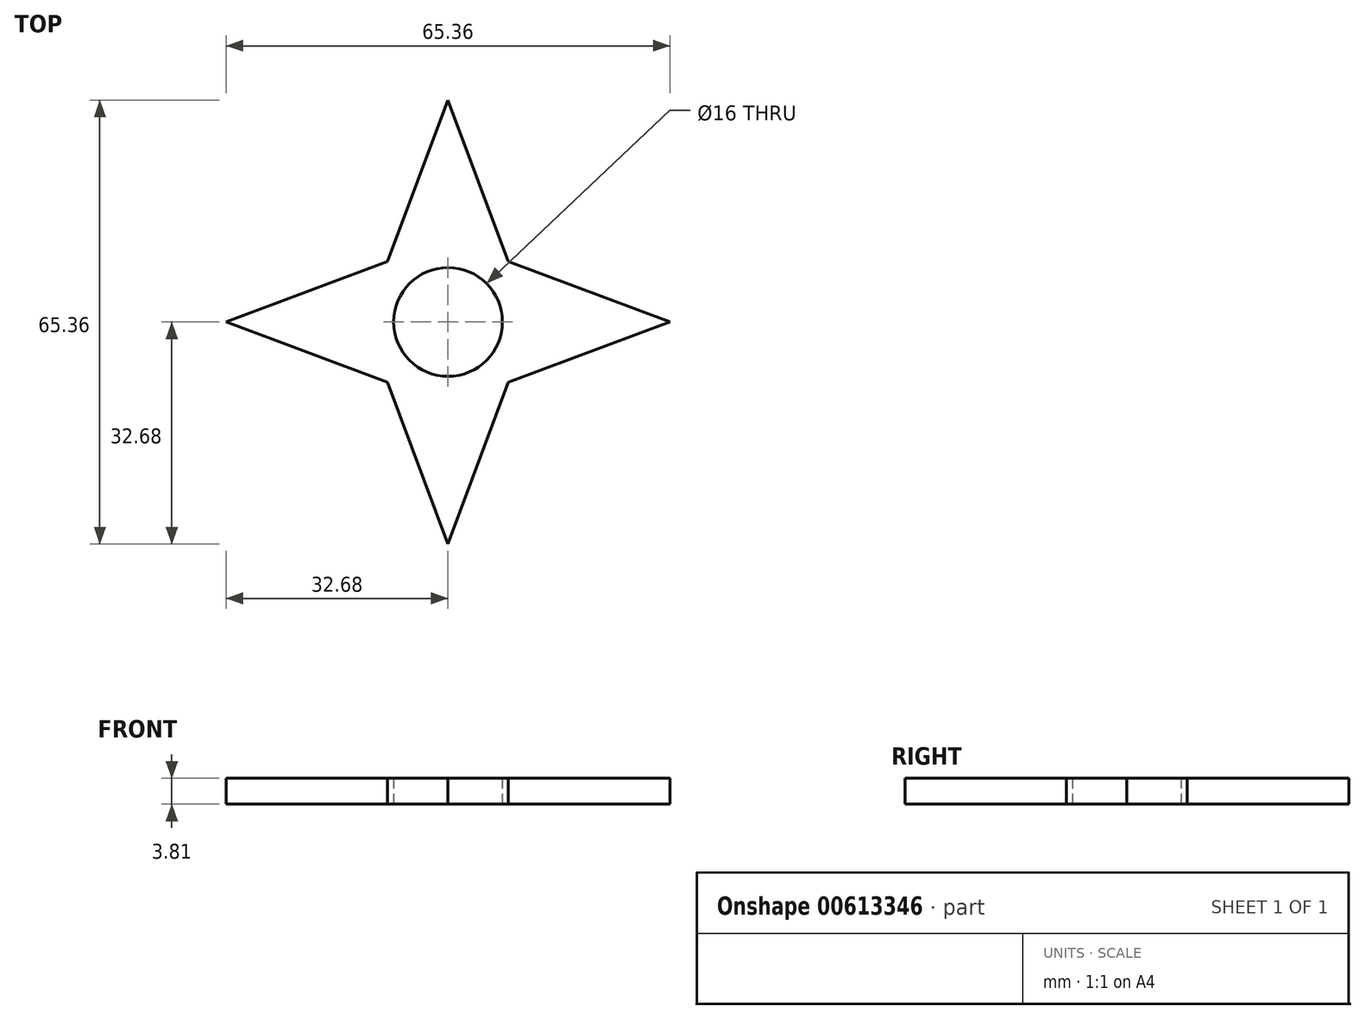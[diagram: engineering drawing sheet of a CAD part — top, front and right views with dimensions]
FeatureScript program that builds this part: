
annotation { "Feature Type Name" : "Feature", "Feature Type Description" : "" }
export const myFeature = defineFeature(function(context is Context, id is Id, definition is map)
    precondition{}
    {
        {
            var Q0;
            Q0=qCreatedBy(makeId("Top.planeOp"),FACE);
            var sketch = newSketch(context, id + "F0", { "sketchPlane" : qUnion([Q0])});
            skLineSegment(sketch, "E0.bottom", {"start": v(8.9, 8.9) * mm, "end": v(-8.9, 8.9) * mm});
            skLineSegment(sketch, "E0.top", {"start": v(8.9, -8.89) * mm, "end": v(-8.9, -8.89) * mm});
            skLineSegment(sketch, "E0.left", {"start": v(8.9, 8.9) * mm, "end": v(8.9, -8.89) * mm});
            skLineSegment(sketch, "E0.right", {"start": v(-8.9, 8.9) * mm, "end": v(-8.9, -8.89) * mm});
            skPoint(sketch, "E0.middle", {"position": v(0, 0) * mm});
            skLineSegment(sketch, "E1", {"start": v(-8.9, 8.9) * mm, "end": v(0, 32.68) * mm});
            skLineSegment(sketch, "E2", {"start": v(0, 32.68) * mm, "end": v(8.89, 8.9) * mm});
            skLineSegment(sketch, "E3", {"start": v(-8.89, 8.9) * mm, "end": v(-32.68, 0) * mm});
            skLineSegment(sketch, "E4", {"start": v(-32.68, 0) * mm, "end": v(-8.89, -8.9) * mm});
            skLineSegment(sketch, "E5", {"start": v(-8.9, -8.89) * mm, "end": v(0, -32.68) * mm});
            skLineSegment(sketch, "E6", {"start": v(0, -32.68) * mm, "end": v(8.89, -8.9) * mm});
            skLineSegment(sketch, "E7", {"start": v(8.9, -8.89) * mm, "end": v(32.68, 0) * mm});
            skLineSegment(sketch, "E8", {"start": v(32.68, 0) * mm, "end": v(8.9, 8.9) * mm});
            skCircle(sketch, "E9", {"center": v(0, 0) * mm, "radius": 8 * mm});
            skSolve(sketch);
        }
        {
            var Q0;
            Q0=makeQuery(id+"F0.imprint","IMPRINT",FACE,{"disambiguationData":[TD([[makeQuery(id+"F0.imprint","IMPRINT",EDGE,{"derivedFrom":sQuery(id+"F0.wireOp",EDGE,"E0.bottom")}),-1.0]])]});
            var Q1;
            Q1=makeQuery(id+"F0.imprint","IMPRINT",FACE,{"disambiguationData":[TD([[makeQuery(id+"F0.imprint","IMPRINT",EDGE,{"derivedFrom":sQuery(id+"F0.wireOp",EDGE,"E0.right")}),-1.0]])]});
            var Q2;
            Q2=makeQuery(id+"F0.imprint","IMPRINT",FACE,{"disambiguationData":[TD([[makeQuery(id+"F0.imprint","IMPRINT",EDGE,{"derivedFrom":sQuery(id+"F0.wireOp",EDGE,"E0.top")}),1.0]])]});
            var Q3;
            Q3=makeQuery(id+"F0.imprint","IMPRINT",FACE,{"disambiguationData":[TD([[makeQuery(id+"F0.imprint","IMPRINT",EDGE,{"derivedFrom":sQuery(id+"F0.wireOp",EDGE,"E0.left")}),1.0]])]});
            var Q4;
            Q4=makeQuery(id+"F0.imprint","IMPRINT",FACE,{"disambiguationData":[TD([[makeQuery(id+"F0.imprint","IMPRINT",EDGE,{"derivedFrom":sQuery(id+"F0.wireOp",EDGE,"E0.bottom")}),1.0]])]});
            extrude(context, id + "F1", {"entities" : qUnion([Q0, Q1, Q2, Q3, Q4]), "depth" : 3.8 * mm, "offsetDistance" : 25.4 * mm});
        }
    });
